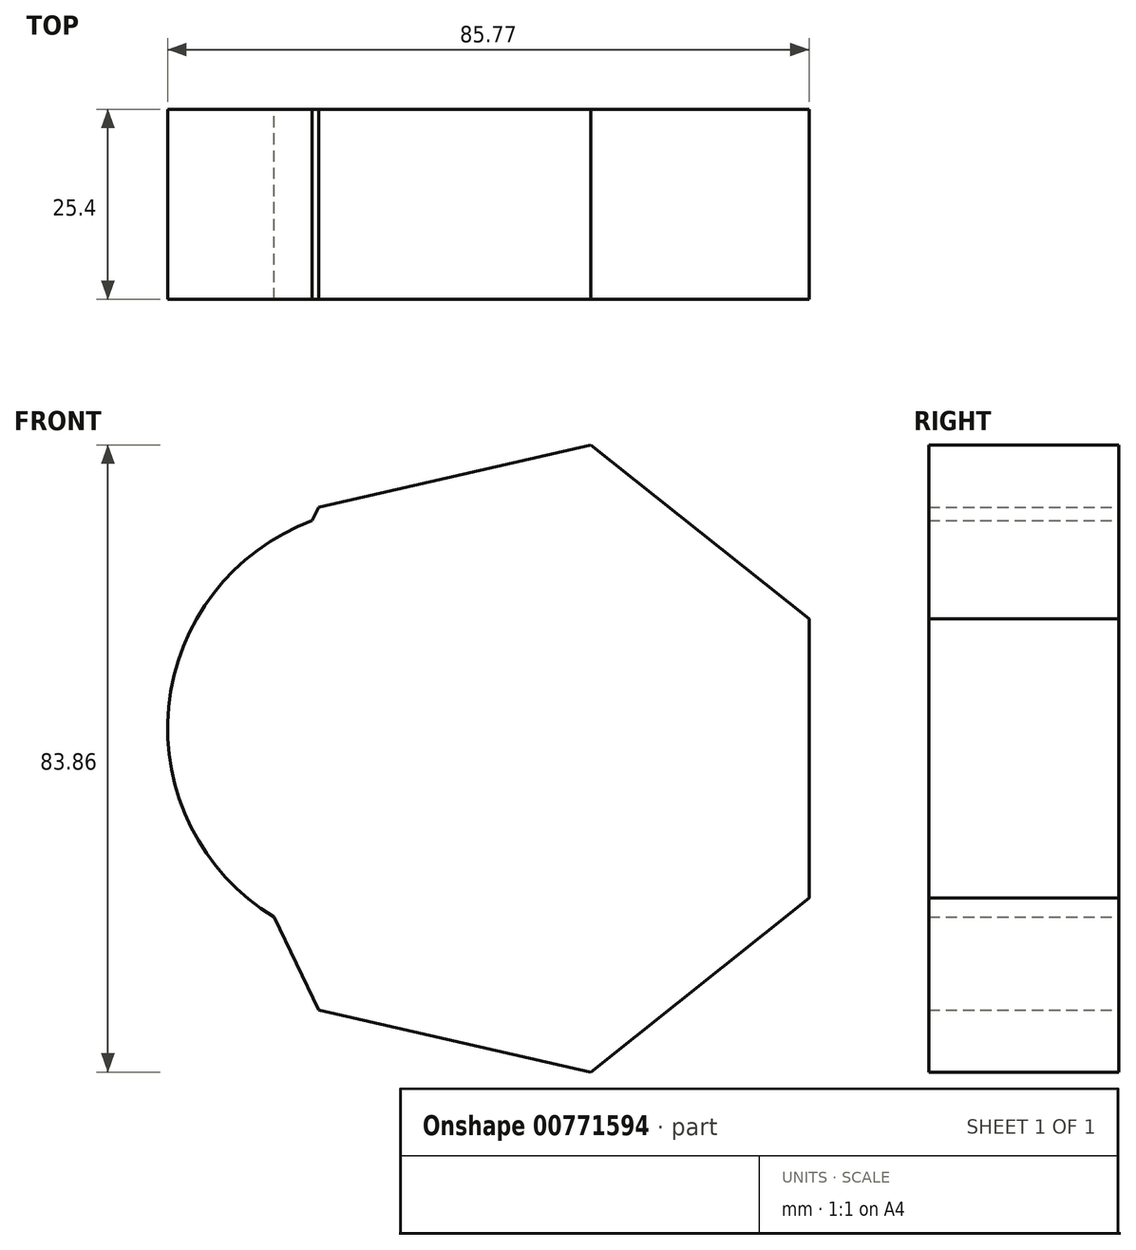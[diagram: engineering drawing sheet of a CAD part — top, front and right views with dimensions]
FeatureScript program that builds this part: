
annotation { "Feature Type Name" : "Feature", "Feature Type Description" : "" }
export const myFeature = defineFeature(function(context is Context, id is Id, definition is map)
    precondition{}
    {
        {
            var Q0;
            Q0=qCreatedBy(makeId("Front.planeOp"),FACE);
            var sketch = newSketch(context, id + "F0", { "sketchPlane" : qUnion([Q0])});
            skCircle(sketch, "E0", {"center": v(-56.2, 37.46) * mm, "radius": 29.57 * mm});
            skCircle(sketch, "E1.cCircle", {"center": v(-38.75, 33.4) * mm, "radius": 38.75 * mm, "construction": true});
            skLineSegment(sketch, "E1.0", {"start": v(0, 52.06) * mm, "end": v(0, 14.74) * mm});
            skLineSegment(sketch, "E1.1", {"start": v(0, 14.74) * mm, "end": v(-29.18, -8.53) * mm});
            skLineSegment(sketch, "E1.2", {"start": v(-29.18, -8.53) * mm, "end": v(-65.57, -0.23) * mm});
            skLineSegment(sketch, "E1.3", {"start": v(-65.57, -0.23) * mm, "end": v(-81.76, 33.4) * mm});
            skLineSegment(sketch, "E1.4", {"start": v(-81.76, 33.4) * mm, "end": v(-65.57, 67.03) * mm});
            skLineSegment(sketch, "E1.5", {"start": v(-65.57, 67.03) * mm, "end": v(-29.18, 75.33) * mm});
            skLineSegment(sketch, "E1.6", {"start": v(-29.18, 75.33) * mm, "end": v(0, 52.06) * mm});
            skPoint(sketch, "E1.0.midPoint", {"position": v(0, 33.4) * mm});
            skSolve(sketch);
        }
        {
            var Q0;
            Q0=makeQuery(id+"F0.imprint","IMPRINT",FACE,{"disambiguationData":[TD([[makeQuery(id+"F0.imprint","IMPRINT",EDGE,{"derivedFrom":sQuery(id+"F0.wireOp",EDGE,"E0")}),1.0]])]});
            extrude(context, id + "F1", {"entities" : qUnion([Q0]), "depth" : 25.4 * mm, "offsetDistance" : 25.4 * mm});
        }
        {
            var Q0;
            Q0 = qSketchRegion(id + "F0", true);
            extrude(context, id + "F2", {"entities" : qUnion([Q0]), "operationType" : NewBodyOperationType.ADD, "depth" : 25.4 * mm, "offsetDistance" : 25.4 * mm});
        }
    });
